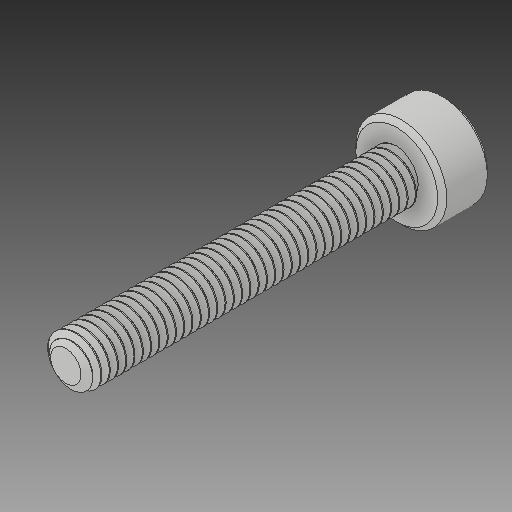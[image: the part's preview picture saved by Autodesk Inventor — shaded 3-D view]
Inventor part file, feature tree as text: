
AUTODESK INVENTOR PART (.ipt)
format: ipt  version: 2018 (Build 220112000, 112)  size: 1,432,064 bytes
history: native  units: in
note: dims shown in document units (in); Inventor stores cm internally (conversion verified against a paired STEP export)
features: chamfer x1
ambient origin geometry x8: Origin, YZ Plane, XZ Plane, XY Plane, X Axis, Y Axis, Z Axis, Center Point
bodies: Solid1 (feature_tree)
feature tree (1):
  chamfer  "Chamfer1"  [1 undecoded]
note: 1 required parameter value undecoded (feature->parameter linkage not recoverable at this tier; creation-order binding heuristic only, values carry confidence <= 0.55)
